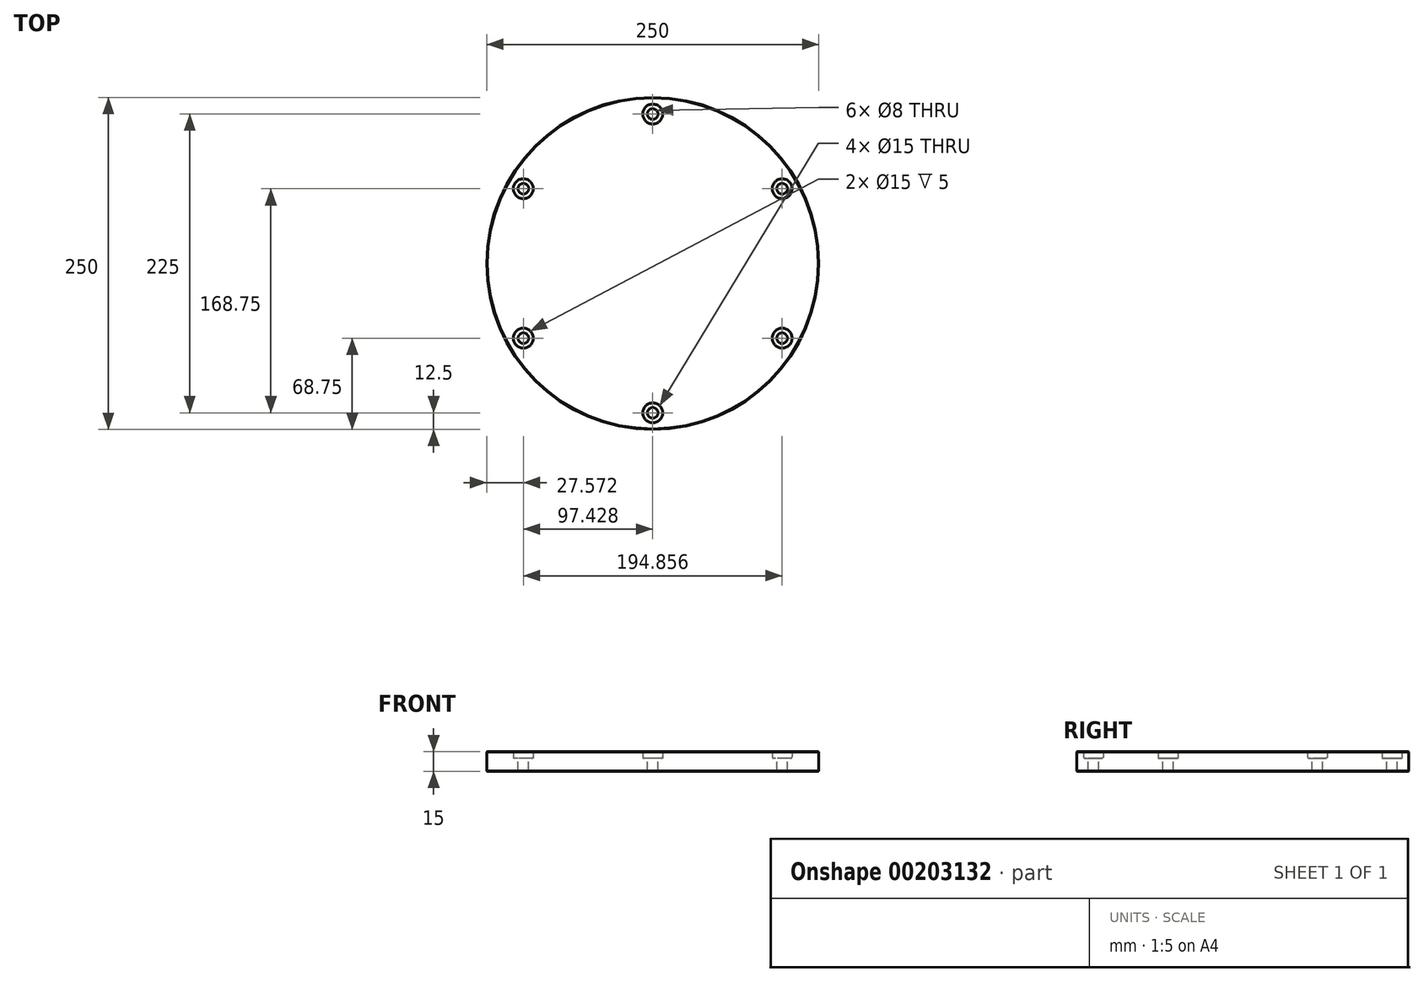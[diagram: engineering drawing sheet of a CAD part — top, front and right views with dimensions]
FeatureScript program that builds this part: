
annotation { "Feature Type Name" : "Feature", "Feature Type Description" : "" }
export const myFeature = defineFeature(function(context is Context, id is Id, definition is map)
    precondition{}
    {
        {
            var Q0;
            Q0=qCreatedBy(makeId("Top.planeOp"),FACE);
            var sketch = newSketch(context, id + "F0", { "sketchPlane" : qUnion([Q0])});
            skCircle(sketch, "E0.cCircle", {"center": v(0, 0) * mm, "radius": 129.9 * mm, "construction": true});
            skLineSegment(sketch, "E0.0", {"start": v(0, 259.8) * mm, "end": v(225, -129.9) * mm});
            skLineSegment(sketch, "E0.1", {"start": v(225, -129.9) * mm, "end": v(-225, -129.9) * mm});
            skLineSegment(sketch, "E0.2", {"start": v(-225, -129.9) * mm, "end": v(0, 259.8) * mm});
            skPoint(sketch, "E0.0.midPoint", {"position": v(112.5, 64.95) * mm});
            skCircle(sketch, "E1", {"center": v(0, 0) * mm, "radius": 125 * mm});
            skSolve(sketch);
        }
        {
            var Q0;
            Q0=makeQuery(id+"F0.imprint","IMPRINT",FACE,{"disambiguationData":[TD([[makeQuery(id+"F0.imprint","IMPRINT",EDGE,{"derivedFrom":sQuery(id+"F0.wireOp",EDGE,"E1")}),1.0]])]});
            extrude(context, id + "F1", {"entities" : qUnion([Q0]), "depth" : 10 * mm});
        }
        {
            var Q0;
            Q0=makeQuery(id+"F1.opExtrude","CAP_FACE",FACE,{"disambiguationData":[OSD([sQuery(id+"F0.wireOp",EDGE,"E1")])],"isStart":false});
            var sketch = newSketch(context, id + "F2", { "sketchPlane" : qUnion([Q0])});
            skLineSegment(sketch, "E2", {"start": v(0, 156.93) * mm, "end": v(0, -175.5) * mm, "construction": true});
            skLineSegment(sketch, "E3", {"start": v(-161.77, 0) * mm, "end": v(255.4, 0) * mm, "construction": true});
            skLineSegment(sketch, "E4", {"start": v(0, 0) * mm, "end": v(-157.67, 91.03) * mm, "construction": true});
            skLineSegment(sketch, "E5", {"start": v(0, 0) * mm, "end": v(0, 196.8) * mm, "construction": true});
            skCircle(sketch, "E6", {"center": v(0, 0) * mm, "radius": 112.5 * mm, "construction": true});
            skPoint(sketch, "E7", {"position": v(-97.43, 56.25) * mm});
            skPoint(sketch, "E8", {"position": v(0, 112.5) * mm});
            skCircle(sketch, "E9", {"center": v(-97.43, 56.25) * mm, "radius": 7.5 * mm});
            skCircle(sketch, "E10", {"center": v(0, 112.5) * mm, "radius": 7.5 * mm});
            skLineSegment(sketch, "E11.MirrorCS", {"start": v(0, 0) * mm, "end": v(157.67, 91.03) * mm, "construction": true});
            skCircle(sketch, "E12.MirrorC", {"center": v(97.43, 56.25) * mm, "radius": 7.5 * mm});
            skLineSegment(sketch, "E13.MirrorCS", {"start": v(0, 0) * mm, "end": v(-157.67, -91.03) * mm, "construction": true});
            skLineSegment(sketch, "E14.MirrorCS", {"start": v(0, 0) * mm, "end": v(0, -196.8) * mm, "construction": true});
            skLineSegment(sketch, "E15.MirrorCS", {"start": v(0, 0) * mm, "end": v(157.67, -91.03) * mm, "construction": true});
            skCircle(sketch, "E16.MirrorC", {"center": v(97.43, -56.25) * mm, "radius": 7.5 * mm});
            skCircle(sketch, "E17.MirrorC", {"center": v(0, -112.5) * mm, "radius": 7.5 * mm});
            skCircle(sketch, "E18.MirrorC", {"center": v(-97.43, -56.25) * mm, "radius": 7.5 * mm});
            skSolve(sketch);
        }
        {
            var Q0;
            Q0=makeQuery(id+"F2.imprint","IMPRINT",FACE,{"disambiguationData":[TD([[makeQuery(id+"F2.imprint","IMPRINT",EDGE,{"derivedFrom":sQuery(id+"F2.wireOp",EDGE,"E9")}),-1.0]])]});
            extrude(context, id + "F3", {"entities" : qUnion([Q0]), "operationType" : NewBodyOperationType.ADD, "depth" : 5 * mm});
        }
        {
            var Q0;
            Q0=makeQuery(id+"F3.opExtrude","CAP_FACE",FACE,{"disambiguationData":[OSD([sQuery(id+"F0.wireOp",EDGE,"E1"),sQuery(id+"F2.wireOp",EDGE,"E9"),sQuery(id+"F2.wireOp",EDGE,"E10"),sQuery(id+"F2.wireOp",EDGE,"E12.MirrorC"),sQuery(id+"F2.wireOp",EDGE,"E16.MirrorC"),sQuery(id+"F2.wireOp",EDGE,"E17.MirrorC"),sQuery(id+"F2.wireOp",EDGE,"E18.MirrorC")])],"isStart":false});
            var sketch = newSketch(context, id + "F4", { "sketchPlane" : qUnion([Q0])});
            skCircle(sketch, "E19", {"center": v(-97.43, 56.25) * mm, "radius": 4 * mm});
            skCircle(sketch, "E20", {"center": v(0, 112.5) * mm, "radius": 4 * mm});
            skCircle(sketch, "E21", {"center": v(97.43, 56.25) * mm, "radius": 4 * mm});
            skCircle(sketch, "E22", {"center": v(97.43, -56.25) * mm, "radius": 4 * mm});
            skCircle(sketch, "E23", {"center": v(0, -112.5) * mm, "radius": 4 * mm});
            skCircle(sketch, "E24", {"center": v(-97.43, -56.25) * mm, "radius": 4 * mm});
            skSolve(sketch);
        }
        {
            var Q0;
            Q0 = qSketchRegion(id + "F4", true);
            extrude(context, id + "F5", {"entities" : qUnion([Q0]), "operationType" : NewBodyOperationType.REMOVE, "endBound" : BoundingType.THROUGH_ALL, "oppositeDirection" : true, "depth" : 25.4 * mm});
        }
        {
            var Q0;
            {var subQ0=sQuery(id+"F0.wireOp",EDGE,"E1");Q0=makeQuery(id+"F3.boolean.opBoolean","MERGE",FACE,{"derivedFrom":[makeQuery(id+"F1.opExtrude","SWEPT_FACE",FACE,{"disambiguationData":[OSD([subQ0])]}),makeQuery(id+"F3.opExtrude","SWEPT_FACE",FACE,{"disambiguationData":[OSD([subQ0])]})]});}
            chamfer(context, id + "F6", {"entities" : qUnion([Q0]), "width" : 0.5 * mm, "tangentPropagation" : true});
        }
        {
            var Q0;
            Q0=makeQuery(id+"F3.opExtrude","CAP_EDGE",EDGE,{"disambiguationData":[OSD([sQuery(id+"F2.wireOp",EDGE,"E9")])],"isStart":true});
            var Q1;
            Q1=makeQuery(id+"F3.opExtrude","CAP_EDGE",EDGE,{"disambiguationData":[OSD([sQuery(id+"F2.wireOp",EDGE,"E10")])],"isStart":true});
            var Q2;
            Q2=makeQuery(id+"F3.opExtrude","CAP_EDGE",EDGE,{"disambiguationData":[OSD([sQuery(id+"F2.wireOp",EDGE,"E12.MirrorC")])],"isStart":true});
            var Q3;
            Q3=makeQuery(id+"F3.opExtrude","CAP_EDGE",EDGE,{"disambiguationData":[OSD([sQuery(id+"F2.wireOp",EDGE,"E16.MirrorC")])],"isStart":true});
            var Q4;
            Q4=makeQuery(id+"F3.opExtrude","CAP_EDGE",EDGE,{"disambiguationData":[OSD([sQuery(id+"F2.wireOp",EDGE,"E17.MirrorC")])],"isStart":true});
            var Q5;
            Q5=makeQuery(id+"F3.opExtrude","CAP_EDGE",EDGE,{"disambiguationData":[OSD([sQuery(id+"F2.wireOp",EDGE,"E18.MirrorC")])],"isStart":true});
            fillet(context, id + "F7", {"entities" : qUnion([Q0, Q1, Q2, Q3, Q4, Q5]), "radius" : 1 * mm, "tangentPropagation" : true, "allowEdgeOverflow" : false});
        }
    });
